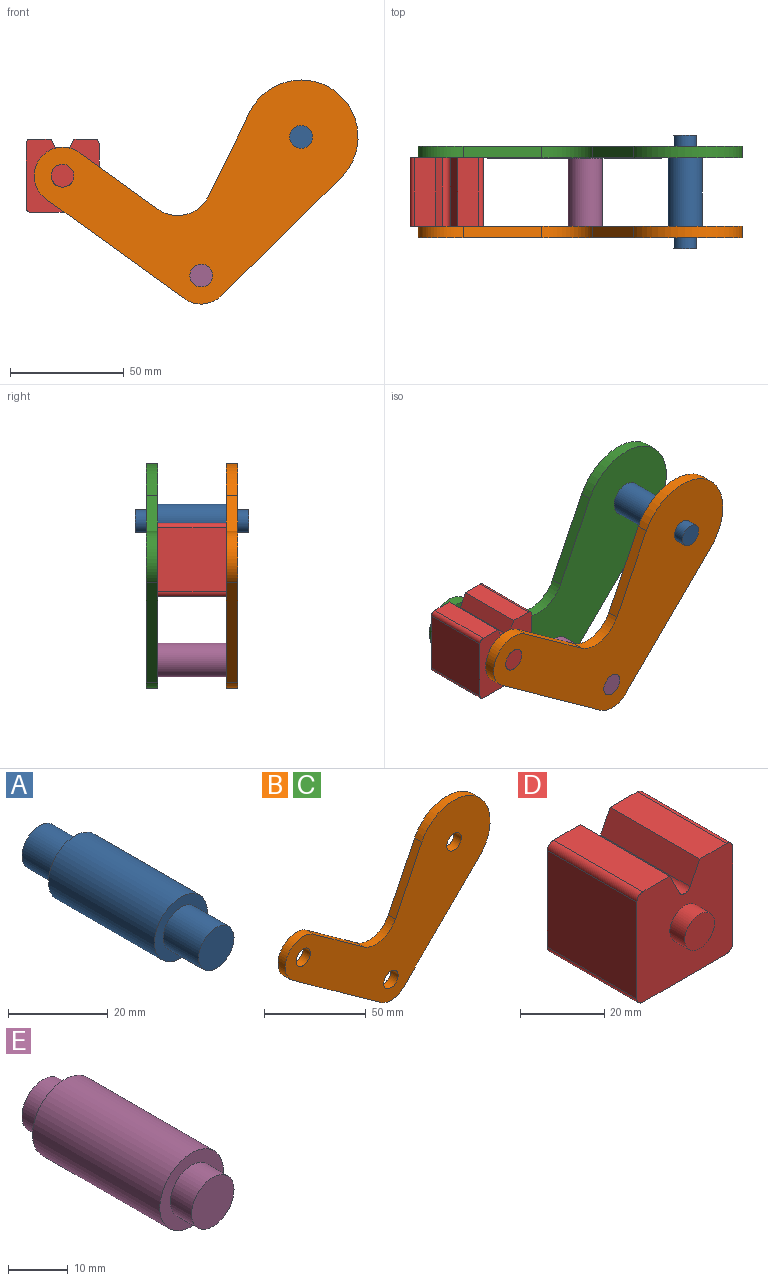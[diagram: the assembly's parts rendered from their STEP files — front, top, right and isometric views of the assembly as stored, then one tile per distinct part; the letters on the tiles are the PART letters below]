
ASSEMBLY  parts=5 mates=3
PART A: 7 faces, bbox 15x50x15 mm
  f0: cylinder r=7.5mm len=30mm, axis (0,-1,0), area 1413.7mm2, adj f2,f5
  f1: cylinder r=5mm len=10mm, axis (0,1,0), area 314.2mm2, adj f2,f3
  f2: plane 15x15mm, normal (0,-1,0), area 98.2mm2, adj f0,f1
  f3: plane 10x10mm, normal (0,-1,0), area 78.5mm2, adj f1
  f4: cylinder r=5mm len=10mm, axis (0,-1,0), area 314.2mm2, adj f5,f6
  f5: plane 15x15mm, normal (0,1,0), area 98.2mm2, adj f0,f4
  f6: plane 10x10mm, normal (0,1,0), area 78.5mm2, adj f4
PART B: 13 faces, bbox 142.2x5x98.4 mm
  f0: plane 52.61x51.97mm, normal (0.7,0,-0.71), area 369.8mm2, adj f1,f9,f11,f12
  f1: cylinder r=25mm len=47.44mm, axis (0,-1,0), area 434.6mm2, adj f0,f2,f11,f12
  f2: plane 37.17x18.26mm, normal (-0.9,0,0.44), area 207.1mm2, adj f1,f3,f11,f12
  f3: cylinder r=15mm len=22.23mm, axis (0,-1,0), area 130.4mm2, adj f2,f4,f11,f12
  f4: plane 34.46x24.81mm, normal (0.58,0,0.81), area 212.3mm2, adj f3,f5,f11,f12
  f5: cylinder r=12.5mm len=22.64mm, axis (0,-1,0), area 196.3mm2, adj f4,f6,f11,f12
  f6: plane 60.86x43.82mm, normal (-0.58,0,-0.81), area 375mm2, adj f5,f9,f11,f12
  f7: cylinder r=5mm len=10mm, axis (0,-1,0), area 157.1mm2, adj f11,f12
  f8: cylinder r=5mm len=10mm, axis (0,-1,0), area 157.1mm2, adj f11,f12
  f9: cylinder r=12.5mm len=16.09mm, axis (0,-1,0), area 87.7mm2, adj f0,f6,f11,f12
  f10: cylinder r=5mm len=10mm, axis (0,-1,0), area 157.1mm2, adj f11,f12
  f11: plane 142.19x98.36mm, normal (0,1,0), area 5739.8mm2, adj f0,f1,f2,f3,f4,f5,f6,f7
  f12: plane 142.19x98.36mm, normal (0,-1,0), area 5739.8mm2, adj f0,f1,f2,f3,f4,f5,f6,f7
PART C: same geometry as B
PART D: 18 faces, bbox 32.1x40x32.1 mm
  f0: plane 30x6.42mm, normal (0.89,0,0.45), area 215.4mm2, adj f4,f6,f10,f13
  f1: plane 30x6.42mm, normal (-0.89,0,0.45), area 215.4mm2, adj f2,f4,f10,f13
  f2: plane 30x9.04mm, normal (0,0,1), area 271.2mm2, adj f1,f4,f10,f14
  f3: plane 30x28.08mm, normal (1,0,0), area 842.3mm2, adj f4,f10,f14,f15
  f4: plane 32.08x32.08mm, normal (0,-1,0), area 900.6mm2, adj f0,f1,f2,f3,f5,f6,f7,f9
  f5: plane 30x28.08mm, normal (0,0,-1), area 842.3mm2, adj f4,f10,f15,f16
  f6: plane 30x9.04mm, normal (0,0,1), area 271.2mm2, adj f0,f4,f10,f17
  f7: plane 30x28.08mm, normal (-1,0,0), area 842.3mm2, adj f4,f10,f16,f17
  f8: plane 10x10mm, normal (0,-1,0), area 78.5mm2, adj f9
  f9: cylinder r=5mm len=10mm, axis (0,1,0), area 157.1mm2, adj f4,f8
  f10: plane 32.08x32.08mm, normal (0,1,0), area 900.6mm2, adj f0,f1,f2,f3,f5,f6,f7,f12
  f11: plane 10x10mm, normal (0,1,0), area 78.5mm2, adj f12
  f12: cylinder r=5mm len=10mm, axis (0,-1,0), area 157.1mm2, adj f10,f11
  f13: cylinder r=2mm len=30mm, axis (0,1,0), area 132.9mm2, adj f0,f1,f4,f10
  f14: cylinder r=2mm len=30mm, axis (0,1,0), area 94.2mm2, adj f2,f3,f4,f10
  f15: cylinder r=2mm len=30mm, axis (0,-1,0), area 94.2mm2, adj f3,f4,f5,f10
  f16: cylinder r=2mm len=30mm, axis (0,1,0), area 94.2mm2, adj f4,f5,f7,f10
  f17: cylinder r=2mm len=30mm, axis (0,-1,0), area 94.2mm2, adj f4,f6,f7,f10
PART E: 7 faces, bbox 15x40x15 mm
  f0: cylinder r=7.5mm len=30mm, axis (0,-1,0), area 1413.7mm2, adj f2,f5
  f1: cylinder r=5mm len=10mm, axis (0,-1,0), area 157.1mm2, adj f2,f3
  f2: plane 15x15mm, normal (0,-1,0), area 98.2mm2, adj f0,f1
  f3: plane 10x10mm, normal (0,-1,0), area 78.5mm2, adj f1
  f4: cylinder r=5mm len=10mm, axis (0,1,0), area 157.1mm2, adj f5,f6
  f5: plane 15x15mm, normal (0,1,0), area 98.2mm2, adj f0,f4
  f6: plane 10x10mm, normal (0,1,0), area 78.5mm2, adj f4
PLACE A t=(0,-20,0)mm fixed
PLACE B t=(0,-20,0)mm
PLACE C t=(0,15,0)mm
PLACE D t=(0,-20,0)mm
PLACE E t=(0,-20,0)mm
MATE fastened B.f7 <-> E.f0  axis (0,1,0) through (-43.82,-15,-60.86)mm
MATE fastened A.f0 <-> C.f1  axis (0,1,0) through (0,15,0)mm
MATE revolute D.f9 <-> B.f5  axis (0,-1,0) through (-104.69,-15,-17.04)mm
